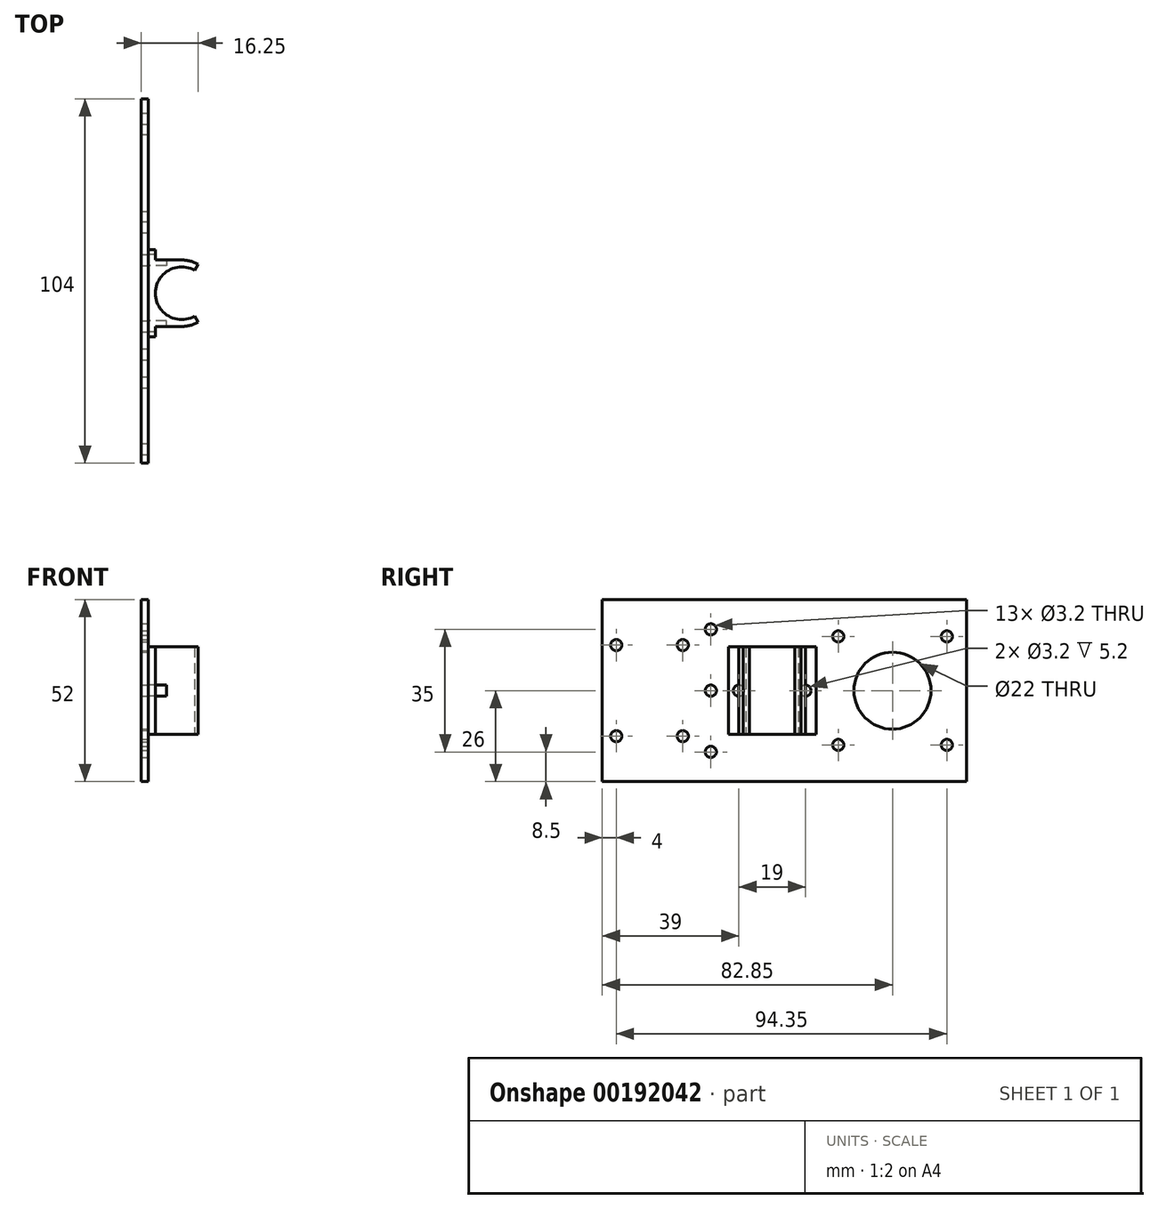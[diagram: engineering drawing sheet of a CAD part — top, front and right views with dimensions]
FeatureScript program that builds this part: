
annotation { "Feature Type Name" : "Feature", "Feature Type Description" : "" }
export const myFeature = defineFeature(function(context is Context, id is Id, definition is map)
    precondition{}
    {
        {
            var Q0;
            Q0=qCreatedBy(makeId("Top.planeOp"),FACE);
            var sketch = newSketch(context, id + "F0", { "sketchPlane" : qUnion([Q0])});
            skCircle(sketch, "E0", {"center": v(-10.5, 17.5) * mm, "radius": 4 * mm, "construction": true});
            skCircle(sketch, "E1.MirrorC", {"center": v(-10.5, -17.5) * mm, "radius": 4 * mm, "construction": true});
            skCircle(sketch, "E2", {"center": v(-10.5, 17.5) * mm, "radius": 7.5 * mm, "construction": true});
            skCircle(sketch, "E3.MirrorC", {"center": v(-10.5, -17.5) * mm, "radius": 7.5 * mm, "construction": true});
            skLineSegment(sketch, "E4.bottom", {"start": v(7.5, 3) * mm, "end": v(-7.5, 3) * mm, "construction": true});
            skLineSegment(sketch, "E4.top", {"start": v(7.5, -3) * mm, "end": v(-7.5, -3) * mm, "construction": true});
            skLineSegment(sketch, "E4.left", {"start": v(7.5, 3) * mm, "end": v(7.5, -3) * mm, "construction": true});
            skLineSegment(sketch, "E4.right", {"start": v(-7.5, 3) * mm, "end": v(-7.5, -3) * mm, "construction": true});
            skPoint(sketch, "E4.middle", {"position": v(0, 0) * mm});
            skSolve(sketch);
        }
        {
            var Q0;
            Q0=qCreatedBy(makeId("Top.planeOp"),FACE);
            var sketch = newSketch(context, id + "F1", { "sketchPlane" : qUnion([Q0])});
            skPoint(sketch, "E5.0", {"position": v(-10.5, 17.5) * mm});
            skLineSegment(sketch, "E6", {"start": v(-20, 17.5) * mm, "end": v(-20, 30) * mm});
            skLineSegment(sketch, "E7", {"start": v(-20, 30) * mm, "end": v(-18, 30) * mm});
            skLineSegment(sketch, "E8", {"start": v(-18, 30) * mm, "end": v(-18, 27) * mm});
            skLineSegment(sketch, "E9", {"start": v(-18, 27) * mm, "end": v(-10.5, 27) * mm});
            skCircle(sketch, "E10.0", {"center": v(-10.5, 17.5) * mm, "radius": 7.5 * mm, "construction": true});
            skArc(sketch, "E11", {"start": v(-6.75, 24) * mm, "mid": v(-14.25, 24) * mm, "end": v(-18, 17.5) * mm});
            skArc(sketch, "E12", {"start": v(-10.5, 27) * mm, "mid": v(-8.04, 26.68) * mm, "end": v(-5.75, 25.73) * mm});
            skLineSegment(sketch, "E13", {"start": v(-5.75, 25.73) * mm, "end": v(-6.75, 24) * mm});
            skLineSegment(sketch, "E14.bottom", {"start": v(-18, 30) * mm, "end": v(-15.6, 30) * mm, "construction": true});
            skLineSegment(sketch, "E14.top", {"start": v(-18, 24) * mm, "end": v(-15.6, 24) * mm, "construction": true});
            skLineSegment(sketch, "E14.left", {"start": v(-18, 30) * mm, "end": v(-18, 24) * mm, "construction": true});
            skLineSegment(sketch, "E14.right", {"start": v(-15.6, 30) * mm, "end": v(-15.6, 24) * mm, "construction": true});
            skLineSegment(sketch, "E15", {"start": v(-20, 17.5) * mm, "end": v(-18, 17.5) * mm, "construction": true});
            skLineSegment(sketch, "E16.MirrorCS", {"start": v(-20, 17.5) * mm, "end": v(-20, 5) * mm});
            skLineSegment(sketch, "E17.MirrorCS", {"start": v(-20, 5) * mm, "end": v(-18, 5) * mm});
            skLineSegment(sketch, "E18.MirrorCS", {"start": v(-18, 8) * mm, "end": v(-10.5, 8) * mm});
            skLineSegment(sketch, "E19.MirrorCS", {"start": v(-18, 5) * mm, "end": v(-18, 11) * mm, "construction": true});
            skLineSegment(sketch, "E20.MirrorCS", {"start": v(-15.6, 5) * mm, "end": v(-15.6, 11) * mm, "construction": true});
            skLineSegment(sketch, "E21.MirrorCS", {"start": v(-18, 5) * mm, "end": v(-15.6, 5) * mm, "construction": true});
            skLineSegment(sketch, "E22.MirrorCS", {"start": v(-18, 11) * mm, "end": v(-15.6, 11) * mm, "construction": true});
            skLineSegment(sketch, "E23.MirrorCS", {"start": v(-18, 5) * mm, "end": v(-18, 8) * mm});
            skArc(sketch, "E24.MirrorCS", {"start": v(-6.75, 11) * mm, "mid": v(-14.25, 11) * mm, "end": v(-18, 17.5) * mm});
            skArc(sketch, "E25.MirrorCS", {"start": v(-10.5, 8) * mm, "mid": v(-8.04, 8.32) * mm, "end": v(-5.75, 9.27) * mm});
            skLineSegment(sketch, "E26.MirrorCS", {"start": v(-5.75, 9.27) * mm, "end": v(-6.75, 11) * mm});
            skLineSegment(sketch, "E27.MirrorCS", {"start": v(-20, -17.5) * mm, "end": v(-18, -17.5) * mm, "construction": true});
            skLineSegment(sketch, "E28.MirrorCS", {"start": v(-18, -5) * mm, "end": v(-15.6, -5) * mm, "construction": true});
            skLineSegment(sketch, "E29.MirrorCS", {"start": v(-20, -30) * mm, "end": v(-18, -30) * mm});
            skLineSegment(sketch, "E30.MirrorCS", {"start": v(-5.75, -25.73) * mm, "end": v(-6.75, -24) * mm});
            skLineSegment(sketch, "E31.MirrorCS", {"start": v(-18, -11) * mm, "end": v(-15.6, -11) * mm, "construction": true});
            skLineSegment(sketch, "E32.MirrorCS", {"start": v(-18, -24) * mm, "end": v(-15.6, -24) * mm, "construction": true});
            skLineSegment(sketch, "E33.MirrorCS", {"start": v(-20, -5) * mm, "end": v(-18, -5) * mm});
            skLineSegment(sketch, "E34.MirrorCS", {"start": v(-18, -30) * mm, "end": v(-15.6, -30) * mm, "construction": true});
            skLineSegment(sketch, "E35.MirrorCS", {"start": v(-5.75, -9.27) * mm, "end": v(-6.75, -11) * mm});
            skLineSegment(sketch, "E36.MirrorCS", {"start": v(-18, -30) * mm, "end": v(-18, -27) * mm});
            skLineSegment(sketch, "E37.MirrorCS", {"start": v(-18, -5) * mm, "end": v(-18, -8) * mm});
            skArc(sketch, "E38.MirrorCS", {"start": v(-6.75, -24) * mm, "mid": v(-14.25, -24) * mm, "end": v(-18, -17.5) * mm});
            skArc(sketch, "E39.MirrorCS", {"start": v(-6.75, -11) * mm, "mid": v(-14.25, -11) * mm, "end": v(-18, -17.5) * mm});
            skLineSegment(sketch, "E40.MirrorCS", {"start": v(-20, -17.5) * mm, "end": v(-20, -30) * mm});
            skArc(sketch, "E41.MirrorCS", {"start": v(-10.5, -8) * mm, "mid": v(-8.04, -8.32) * mm, "end": v(-5.75, -9.27) * mm});
            skLineSegment(sketch, "E42.MirrorCS", {"start": v(-18, -27) * mm, "end": v(-10.5, -27) * mm});
            skArc(sketch, "E43.MirrorCS", {"start": v(-10.5, -27) * mm, "mid": v(-8.04, -26.68) * mm, "end": v(-5.75, -25.73) * mm});
            skLineSegment(sketch, "E44.MirrorCS", {"start": v(-18, -30) * mm, "end": v(-18, -24) * mm, "construction": true});
            skLineSegment(sketch, "E45.MirrorCS", {"start": v(-15.6, -30) * mm, "end": v(-15.6, -24) * mm, "construction": true});
            skLineSegment(sketch, "E46.MirrorCS", {"start": v(-15.6, -5) * mm, "end": v(-15.6, -11) * mm, "construction": true});
            skLineSegment(sketch, "E47.MirrorCS", {"start": v(-18, -8) * mm, "end": v(-10.5, -8) * mm});
            skLineSegment(sketch, "E48.MirrorCS", {"start": v(-18, -5) * mm, "end": v(-18, -11) * mm, "construction": true});
            skCircle(sketch, "E49.MirrorC", {"center": v(-10.5, -17.5) * mm, "radius": 7.5 * mm, "construction": true});
            skLineSegment(sketch, "E50.MirrorCS", {"start": v(-20, -17.5) * mm, "end": v(-20, -5) * mm});
            skSolve(sketch);
        }
        {
            var Q0;
            Q0=qCreatedBy(makeId("Right.planeOp"),FACE);
            var sketch = newSketch(context, id + "F2", { "sketchPlane" : qUnion([Q0])});
            skPoint(sketch, "E51.0", {"position": v(27, 0) * mm});
            skPoint(sketch, "E52.0", {"position": v(8, 0) * mm});
            skPoint(sketch, "E53.0", {"position": v(-8, 0) * mm});
            skPoint(sketch, "E54.0", {"position": v(-27, 0) * mm});
            skCircle(sketch, "E55", {"center": v(27, 0) * mm, "radius": 1.6 * mm});
            skCircle(sketch, "E56", {"center": v(8, 0) * mm, "radius": 1.6 * mm});
            skLineSegment(sketch, "E57", {"start": v(-27, 13) * mm, "end": v(-27, -13) * mm, "construction": true});
            skLineSegment(sketch, "E58", {"start": v(-8, 13) * mm, "end": v(-8, -13) * mm, "construction": true});
            skCircle(sketch, "E59", {"center": v(-8, 13) * mm, "radius": 1.6 * mm});
            skCircle(sketch, "E60", {"center": v(-27, 13) * mm, "radius": 1.6 * mm});
            skCircle(sketch, "E61", {"center": v(-27, -13) * mm, "radius": 1.6 * mm});
            skCircle(sketch, "E62", {"center": v(-8, -13) * mm, "radius": 1.6 * mm});
            skSolve(sketch);
        }
        {
            var Q0;
            Q0=sQuery(id+"F1.wireOp",VERTEX,"E16.MirrorCS.start");
            var Q1;
            Q1=sQuery(id+"F1.wireOp",EDGE,"E15");
            cPlane(context, id + "F3", {"entities" : qUnion([Q0, Q1]), "cplaneType" : CPlaneType.LINE_POINT, "offset" : 25 * mm, "width" : 150 * mm, "height" : 150 * mm});
        }
        {
            var Q0;
            Q0=qCreatedBy(id+"F3.planeOp",FACE);
            var sketch = newSketch(context, id + "F4", { "sketchPlane" : qUnion([Q0])});
            skPoint(sketch, "E63.0", {"position": v(30, 0) * mm});
            skPoint(sketch, "E64.0", {"position": v(-30, 0) * mm});
            skLineSegment(sketch, "E65.bottom", {"start": v(-30, 26) * mm, "end": v(30, 26) * mm});
            skLineSegment(sketch, "E65.top", {"start": v(-30, -26) * mm, "end": v(30, -26) * mm});
            skLineSegment(sketch, "E65.left", {"start": v(30, 26) * mm, "end": v(30, -26) * mm, "construction": true});
            skLineSegment(sketch, "E65.right", {"start": v(-30, 26) * mm, "end": v(-30, -26) * mm, "construction": true});
            skCircle(sketch, "E66.0", {"center": v(27, 0) * mm, "radius": 1.6 * mm});
            skCircle(sketch, "E67.0", {"center": v(8, 0) * mm, "radius": 1.6 * mm});
            skCircle(sketch, "E68.0", {"center": v(-8, -13) * mm, "radius": 1.6 * mm});
            skCircle(sketch, "E69.0", {"center": v(-8, 13) * mm, "radius": 1.6 * mm});
            skCircle(sketch, "E70.0", {"center": v(-27, 13) * mm, "radius": 1.6 * mm});
            skCircle(sketch, "E71.0", {"center": v(-27, -13) * mm, "radius": 1.6 * mm});
            skLineSegment(sketch, "E72", {"start": v(30, -26) * mm, "end": v(73, -26) * mm});
            skLineSegment(sketch, "E73", {"start": v(73, -26) * mm, "end": v(73, 26) * mm});
            skLineSegment(sketch, "E74", {"start": v(73, 26) * mm, "end": v(30, 26) * mm});
            skLineSegment(sketch, "E75", {"start": v(73, 0) * mm, "end": v(30.7, 0) * mm, "construction": true});
            skPoint(sketch, "E75.endSnap0", {"position": v(73, 0) * mm});
            skLineSegment(sketch, "E76.bottom", {"start": v(67.35, 15.5) * mm, "end": v(36.35, 15.5) * mm, "construction": true});
            skLineSegment(sketch, "E76.top", {"start": v(67.35, -15.5) * mm, "end": v(36.35, -15.5) * mm, "construction": true});
            skLineSegment(sketch, "E76.left", {"start": v(67.35, 15.5) * mm, "end": v(67.35, -15.5) * mm, "construction": true});
            skLineSegment(sketch, "E76.right", {"start": v(36.35, 15.5) * mm, "end": v(36.35, -15.5) * mm, "construction": true});
            skPoint(sketch, "E76.middle", {"position": v(51.85, 0) * mm});
            skCircle(sketch, "E77", {"center": v(67.35, 15.5) * mm, "radius": 1.6 * mm});
            skCircle(sketch, "E78", {"center": v(67.35, -15.5) * mm, "radius": 1.6 * mm});
            skCircle(sketch, "E79", {"center": v(36.35, -15.5) * mm, "radius": 1.6 * mm});
            skCircle(sketch, "E80", {"center": v(36.35, 15.5) * mm, "radius": 1.6 * mm});
            skCircle(sketch, "E81", {"center": v(51.85, 0) * mm, "radius": 11 * mm});
            skLineSegment(sketch, "E82", {"start": v(0, 0) * mm, "end": v(-43.16, 0) * mm, "construction": true});
            skLineSegment(sketch, "E83", {"start": v(0, 0) * mm, "end": v(14.7, 0) * mm, "construction": true});
            skLineSegment(sketch, "E84", {"start": v(-30, -26) * mm, "end": v(-31, -26) * mm});
            skLineSegment(sketch, "E85", {"start": v(-31, -26) * mm, "end": v(-31, 26) * mm});
            skLineSegment(sketch, "E86", {"start": v(-31, 26) * mm, "end": v(-30, 26) * mm});
            skCircle(sketch, "E87", {"center": v(0, -17.5) * mm, "radius": 1.6 * mm});
            skCircle(sketch, "E88.MirrorC", {"center": v(0, 17.5) * mm, "radius": 1.6 * mm});
            skCircle(sketch, "E89", {"center": v(0, 0) * mm, "radius": 1.6 * mm});
            skSolve(sketch);
        }
        {
            var Q0;
            Q0=makeQuery(id+"F1.imprint","IMPRINT",FACE,{"disambiguationData":[TD([[makeQuery(id+"F1.imprint","IMPRINT",EDGE,{"derivedFrom":sQuery(id+"F1.wireOp",EDGE,"E6")}),-1.0]])]});
            extrude(context, id + "F5", {"entities" : qUnion([Q0]), "depth" : 25 * mm, "symmetric" : true});
        }
        {
            var Q0;
            Q0=makeQuery(id+"F5.opExtrude","SWEPT_FACE",FACE,{"disambiguationData":[OSD([sQuery(id+"F1.wireOp",EDGE,"E6"),sQuery(id+"F1.wireOp",EDGE,"E16.MirrorCS")])]});
            var sketch = newSketch(context, id + "F6", { "sketchPlane" : qUnion([Q0])});
            skCircle(sketch, "E90.0", {"center": v(-27, 0) * mm, "radius": 1.6 * mm});
            skCircle(sketch, "E91.0", {"center": v(-8, 0) * mm, "radius": 1.6 * mm});
            skSolve(sketch);
        }
        {
            var Q0;
            Q0 = qSketchRegion(id + "F6", true);
            extrude(context, id + "F7", {"entities" : qUnion([Q0]), "operationType" : NewBodyOperationType.REMOVE, "oppositeDirection" : true, "depth" : (2 + 3.2) * mm});
        }
        {
            var Q0;
            Q0 = qSketchRegion(id + "F4", true);
            extrude(context, id + "F8", {"entities" : qUnion([Q0]), "oppositeDirection" : true, "depth" : 2 * mm});
        }
    });
